# Revit family: Sanitary_Toilets_TOTO-USA-Inc_NEORESTR-RH-Dual-Flush-Toilet-1-0-GPF-0
name_source: partatom
category: Plumbing Fixtures
revit_build: Autodesk Revit 2015 (Build: 20140606_1530(x64)
units: mm (PartAtom-declared; Revit-internal decimal feet)

## types (1)
- MS988CUMFG
    Ambient Temp. = 32 F to 104F
    BIMobject category = Toilets
    BIMobject category code = sanitary-toilets
    BIMobject main category = Sanitary
    BIMobject main category code = sanitary
    Brand url = https://www.totousa.com
    Default Elevation = 4' - 0"
    Description = The NEOREST RH has been designed with a smooth form and beautiful proportions that serves as an accent to interiors and architectural spaces. The design of the RH is characterized by soft curves without sharp corners and the softly rounded silhouette creates a sense of serenity that harmonizes with a wide variety of comfortable spaces.
    Edition number = 1
    IFC Classification = Flow Terminal
    Installation instructions = https://www.totousa.com
    Manufacturer = TOTO
    Manufacturer name = TOTO USA Inc
    Masterformat 2014 Code = 10 28 00
    Masterformat 2014 Description = Toilet, Bath, and Laundry Accessories
    Material = Galaline - TOTO - Reinforced Marble
    Material main = Ceramics
    Model = MS988CUMFG
    Nominal height = 0' - 0"
    Nominal width = 0' - 0"
    OmniClass Code = 23-31 19 00
    OmniClass Description = Toilets
    Product Guid = 8ff6b6dc-0d16-4e30-9392-f43504cb3e10
    Product SKU = toto-ms988cumfg
    Product certification = https://www.totousa.com
    Product data url = https://bimobject.com
    Product family = Urinals
    Product group = NEOREST??
    Product url = https://www.totousa.com
    QR code = http://bimobject.com
    Rated Voltage = 120 V
    Rough-in = 1' - 0"
    Technical description = https://www.totousa.com
    Trap Seal = 0' - 2 1/8"
    Trap diameter = 0' - 2 1/8"
    UNSPSC Code = 30181505
    Uniclass 1.4 Code = L7216
    Uniclass 1.4 Description = Toilets
    Uniclass 2.0 Code = SS-35-65-90
    Uniclass 2.0 Description = Toilet Systems
    Uniclass 2015 Code = SL_35_80_89
    Uniclass 2015 Name = Toilets
    Uniformat II Code = D2030
    Uniformat II Description = Sanitary Waste
    Warranty = Three Year Limited(Residental), One Year Limited(Commecrcial)

## geometry (parser evidence)
native form markers: Blend x4, Sweep x2
no freeform markers — native parametric forms only
